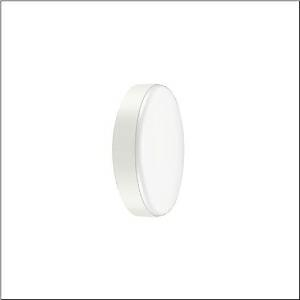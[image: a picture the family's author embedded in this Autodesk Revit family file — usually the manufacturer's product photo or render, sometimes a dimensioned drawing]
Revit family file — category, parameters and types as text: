
# Revit family: round_31_51wc10da42as
name_source: partatom
category: Lighting Fixtures
units: mm (PartAtom-declared; Revit-internal decimal feet)

## family parameters
Cut with Voids When Loaded = No
Host = Face
Light Source = No
Part Type = Normal
Room Calculation Point = No
Round Connector Dimension = Use Diameter
Shared = No

## types (1)
- Round 31 (1 x LED, 2550 lm, 20.5 W, 4000K)
    Apparent Load = 21 VA
    CIE Flux Codes = 44 75 94 94 100
    Color Rendering = 80
    Color Temperature = 4000K
    Default Elevation = 1800 mm
    Description = Round 31, wall and ceiling luminaire, primary optical cover: cover, of PC, opal, light emission: direct distribution, primary light characteristic: symmetric, installation type: surface-mounted, LED, rated luminous flux: 2.550lm, luminous efficacy: 124lm/W, light colour: 840, colour temperature: 4000K, control gear: DALI 2, with terminal, 5-pole, max. 2.5mm², mains connection: 220..240V, AC, 50/60Hz, rated input power: 20.5W, luminaire housing, of PC, traffic white (RAL 9016), diameter: 350mm, brightness and presence sensor, HF sensor, protection rating (complete): IP65, insulation class (complete): insulation class II (safety insulation), certification: CE, impact resistance: IK10, permissible operating ambient temperature: -20..+40°C, permissible storage temperature: -20..+60°C, packaging unit: 1 piece
    Height = 97 mm
    Lamp = 1 x LED
    Lamp Light Flux = 2550 lm
    Lamp Power = 20.5 W
    Lamp count = 1
    Length = 350 mm
    Luminous efficacy = 124 lm/W
    Manufacturer = Siteco
    ModVariant = No
    Model = 51WC10DA42AS
    Mounting Place = Ceiling
    Mounting Type = Surface mounted
    Number of Poles = 1
    OnlyDefault = Yes
    Power Factor = 1
    Product Name = Round 31
    Product group = wall and ceiling luminaire | ceiling mounted
    ProductGroupID = 305
    Protection Class = Protection class II
    Protection Degree = IP 65
    RLX_Detail_Level = 1
    RLX_Emergency_Light_Flux = 0 lm
    RLX_Emergency_Type = 0
    RLX_Emergency_Type_DB = No
    RlxData = <blob elided: 29761 chars, md5=e55a180a>
    Socket = socket
    Standby Power = 0 W
    System Light Flux = 2550 lm
    System Power = 21 W
    Type Comments = Product without accessories
    Type Image = l_1007027.jpg
    URL = http://relux.com
    VarID = ---
    Voltage = 0 V
    Weight = 0.00 kg
    Width = 0 mm  [stored 0 ft]

note: [stored X ft] marks values corroborated as IEEE doubles in the binary element streams (Revit-internal decimal feet)

## geometry (parser evidence)
native form markers: Blend x4, Sweep x10
no freeform markers — native parametric forms only
